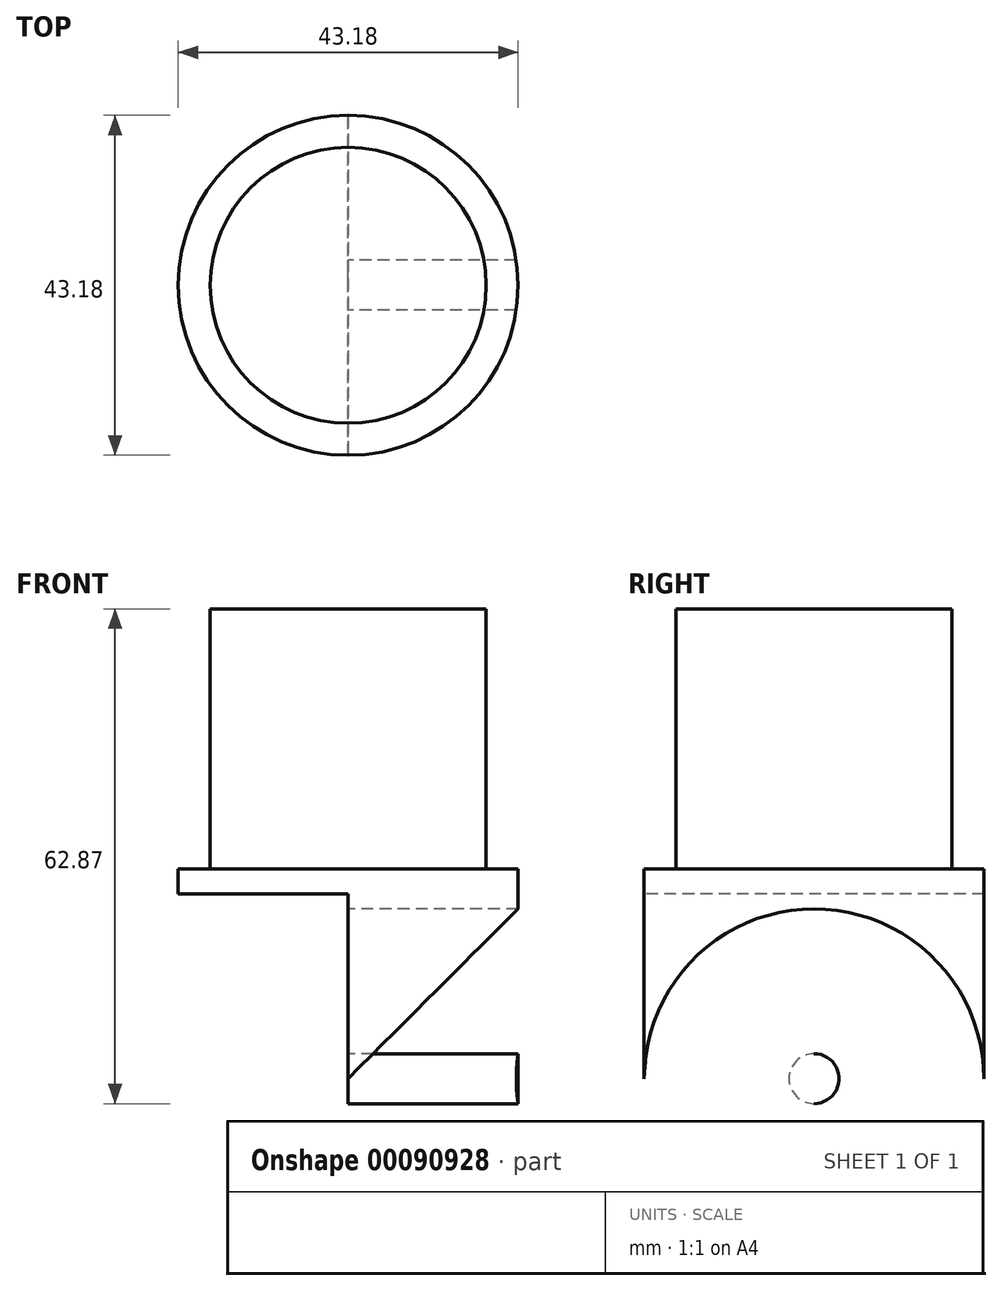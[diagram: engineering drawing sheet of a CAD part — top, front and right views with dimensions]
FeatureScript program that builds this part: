
annotation { "Feature Type Name" : "Feature", "Feature Type Description" : "" }
export const myFeature = defineFeature(function(context is Context, id is Id, definition is map)
    precondition{}
    {
        {
            var Q0;
            Q0=qCreatedBy(makeId("Top.planeOp"),FACE);
            var sketch = newSketch(context, id + "F0", { "sketchPlane" : qUnion([Q0])});
            skCircle(sketch, "E0", {"center": v(0, 0) * mm, "radius": 17.53 * mm});
            skCircle(sketch, "E1", {"center": v(0, 0) * mm, "radius": 21.59 * mm});
            skLineSegment(sketch, "E2", {"start": v(0, 21.59) * mm, "end": v(0, -21.59) * mm});
            skSolve(sketch);
        }
        {
            var Q0;
            Q0=makeQuery(id+"F0.imprint","IMPRINT",FACE,{"disambiguationData":[TD([[makeQuery(id+"F0.imprint","IMPRINT",EDGE,{"derivedFrom":sQuery(id+"F0.wireOp",EDGE,"E0")}),1.0]])]});
            extrude(context, id + "F1", {"entities" : qUnion([Q0]), "depth" : 33.02 * mm});
        }
        {
            var Q0;
            {var subQ0=sQuery(id+"F0.wireOp",EDGE,"E2");var subQ1=sQuery(id+"F0.wireOp",EDGE,"E0");var subQ2=makeQuery(id+"F0.imprint","INTERSECT",VERTEX,{"disambiguationData":[OD(0.0)],"derivedFrom":[subQ1,subQ0]});Q0=makeQuery(id+"F0.imprint","IMPRINT",FACE,{"disambiguationData":[TD([[makeQuery(id+"F0.imprint","IMPRINT",EDGE,{"disambiguationData":[TD([[subQ2,1.0]])],"derivedFrom":subQ1}),1.0]])]});}
            var Q1;
            {var subQ0=sQuery(id+"F0.wireOp",EDGE,"E2");var subQ1=sQuery(id+"F0.wireOp",EDGE,"E0");var subQ2=makeQuery(id+"F0.imprint","INTERSECT",VERTEX,{"disambiguationData":[OD(0.0)],"derivedFrom":[subQ1,subQ0]});Q1=makeQuery(id+"F0.imprint","IMPRINT",FACE,{"disambiguationData":[TD([[makeQuery(id+"F0.imprint","IMPRINT",EDGE,{"disambiguationData":[TD([[subQ2,1.0]])],"derivedFrom":subQ1}),-1.0]])]});}
            extrude(context, id + "F2", {"entities" : qUnion([Q0, Q1]), "operationType" : NewBodyOperationType.ADD, "oppositeDirection" : true, "depth" : 48.26 * mm});
        }
        {
            var Q0;
            {var subQ0=sQuery(id+"F0.wireOp",EDGE,"E2");var subQ1=sQuery(id+"F0.wireOp",EDGE,"E0");var subQ2=makeQuery(id+"F0.imprint","INTERSECT",VERTEX,{"disambiguationData":[OD(0.0)],"derivedFrom":[subQ1,subQ0]});Q0=makeQuery(id+"F0.imprint","IMPRINT",FACE,{"disambiguationData":[TD([[makeQuery(id+"F0.imprint","IMPRINT",EDGE,{"disambiguationData":[TD([[subQ2,-1.0]])],"derivedFrom":subQ1}),-1.0]])]});}
            var Q1;
            {var subQ0=sQuery(id+"F0.wireOp",EDGE,"E2");var subQ1=sQuery(id+"F0.wireOp",EDGE,"E0");var subQ2=makeQuery(id+"F0.imprint","INTERSECT",VERTEX,{"disambiguationData":[OD(0.0)],"derivedFrom":[subQ1,subQ0]});Q1=makeQuery(id+"F0.imprint","IMPRINT",FACE,{"disambiguationData":[TD([[makeQuery(id+"F0.imprint","IMPRINT",EDGE,{"disambiguationData":[TD([[subQ2,-1.0]])],"derivedFrom":subQ1}),1.0]])]});}
            extrude(context, id + "F3", {"entities" : qUnion([Q0, Q1]), "operationType" : NewBodyOperationType.ADD, "oppositeDirection" : true, "depth" : 3.17 * mm});
        }
        {
            var Q0;
            Q0=makeQuery(id+"F2.opExtrude","SWEPT_FACE",FACE,{"disambiguationData":[OSD([sQuery(id+"F0.wireOp",EDGE,"E2")])]});
            var sketch = newSketch(context, id + "F4", { "sketchPlane" : qUnion([Q0])});
            skCircle(sketch, "E3", {"center": v(0, -26.67) * mm, "radius": 21.59 * mm});
            skLineSegment(sketch, "E4", {"start": v(-21.59, -26.67) * mm, "end": v(21.59, -26.67) * mm});
            skPoint(sketch, "E4.endSnap0", {"position": v(21.59, -25.72) * mm});
            skCircle(sketch, "E5", {"center": v(0, -26.67) * mm, "radius": 3.18 * mm});
            skSolve(sketch);
        }
        {
            var Q0;
            {var subQ0=sQuery(id+"F4.wireOp",EDGE,"E5");var subQ1=sQuery(id+"F4.wireOp",EDGE,"E4");var subQ2=makeQuery(id+"F4.imprint","INTERSECT",VERTEX,{"disambiguationData":[OD(0.0)],"derivedFrom":[subQ1,subQ0]});Q0=makeQuery(id+"F4.imprint","IMPRINT",FACE,{"disambiguationData":[TD([[makeQuery(id+"F4.imprint","IMPRINT",EDGE,{"disambiguationData":[TD([[subQ2,-1.0]])],"derivedFrom":subQ1}),-1.0]])]});}
            var Q1;
            {var subQ0=sQuery(id+"F4.wireOp",EDGE,"E5");var subQ1=sQuery(id+"F4.wireOp",EDGE,"E4");var subQ2=makeQuery(id+"F4.imprint","INTERSECT",VERTEX,{"disambiguationData":[OD(0.0)],"derivedFrom":[subQ1,subQ0]});Q1=makeQuery(id+"F4.imprint","IMPRINT",FACE,{"disambiguationData":[TD([[makeQuery(id+"F4.imprint","IMPRINT",EDGE,{"disambiguationData":[TD([[subQ2,-1.0]])],"derivedFrom":subQ1}),1.0]])]});}
            var Q2;
            {var subQ0=sQuery(id+"F4.wireOp",EDGE,"E3");var subQ1=sQuery(id+"F0.wireOp",EDGE,"E2");var subQ5=makeQuery(id+"F2.opExtrude","CAP_EDGE",EDGE,{"disambiguationData":[OSD([subQ1])],"isStart":false});var subQ6=makeQuery(id+"F4.imprint","INTERSECT",VERTEX,{"derivedFrom":[subQ5,subQ0]});Q2=makeQuery(id+"F4.imprint","IMPRINT",FACE,{"disambiguationData":[TD([[makeQuery(id+"F4.imprint","IMPRINT",EDGE,{"disambiguationData":[TD([[subQ6,1.0]])],"derivedFrom":subQ5}),1.0]])]});}
            var Q3;
            {var subQ0=sQuery(id+"F4.wireOp",EDGE,"E3");var subQ1=sQuery(id+"F0.wireOp",EDGE,"E2");var subQ5=makeQuery(id+"F2.opExtrude","CAP_EDGE",EDGE,{"disambiguationData":[OSD([subQ1])],"isStart":false});var subQ6=makeQuery(id+"F4.imprint","INTERSECT",VERTEX,{"derivedFrom":[subQ5,subQ0]});Q3=makeQuery(id+"F4.imprint","IMPRINT",FACE,{"disambiguationData":[TD([[makeQuery(id+"F4.imprint","IMPRINT",EDGE,{"disambiguationData":[TD([[subQ6,-1.0]])],"derivedFrom":subQ5}),1.0]])]});}
            extrude(context, id + "F5", {"entities" : qUnion([Q0, Q1, Q2, Q3]), "operationType" : NewBodyOperationType.REMOVE, "endBound" : BoundingType.THROUGH_ALL, "oppositeDirection" : true, "depth" : 25.4 * mm});
        }
    });
